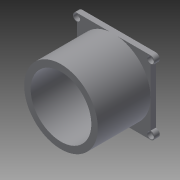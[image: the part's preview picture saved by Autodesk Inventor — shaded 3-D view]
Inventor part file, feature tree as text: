
AUTODESK INVENTOR PART (.ipt)
format: ipt  version: 2013 (Build 170138000, 138)  size: 433,664 bytes
history: native  units: in
note: dims shown in document units (in); Inventor stores cm internally (conversion verified against a paired STEP export)
features: extrude x14, sketch x14, reference x4, projected_geometry x1
ambient origin geometry x8: Origin, YZ Plane, XZ Plane, XY Plane, X Axis, Y Axis, Z Axis, Center Point
bodies: Solid1 (feature_tree)
feature tree (33):
  extrude  "Extrusion1"  Depth=0.1181in
  extrude  "Extrusion14"  Depth=0.1181in
  extrude  "Extrusion15"  Depth=0.1575in TaperAngle=0.0deg
  extrude  "Extrusion17"  Depth=0.0319in
  extrude  "Extrusion18"  Depth=0.1181in
  extrude  "Extrusion19"  Depth=0.1575in TaperAngle=0.0deg
  extrude  "Extrusion20"  Depth=1.5748in TaperAngle=0.0deg
  extrude  "Extrusion21"  Depth=1.811in
  extrude  "Extrusion22"  Depth=0.6339in
  extrude  "Extrusion23"  Depth=0.0394in
  extrude  "Extrusion24"  Depth=0.315in TaperAngle=0.0deg
  extrude  "Extrusion25"  Depth=0.2756in TaperAngle=0.0deg
  extrude  "Extrusion31"  Depth=0.2362in TaperAngle=0.0deg
  extrude  "Extrusion38"  Depth=0.1969in TaperAngle=0.0deg
  sketch  "Sketch40"  dims[d125=0.0394in d126=0.1969in d127=0.0in d128=0.0394in d129=0.1575in d130=0.0in d131=0.0394in d132=0.1181in d133=0.0in d134=0.0394in d135=0.0787in d136=0.0in d137=0.0394in d138=0.0394in d139=0.0in d172=0.1969in d174=0.1969in d175=0.1969in d176=0.1969in d177=0.1181in d178=0.0in d214=0.0in d215=0.1181in d216=0.0in d217=0.9843in d219=0.9843in d220=0.063in d221=0.0in]
  sketch  "Sketch1"  dims[d0=2.2in d2=0.1181in]
  reference  "Reference2"
  reference  "Reference3"
  reference  "Reference4"
  reference  "Reference5"
  sketch  "Sketch15"  dims[d3=0.2362in d4=0.1181in d5=0.2362in d6=1.95in]
  sketch  "Sketch17"  dims[d8=0.1181in d9=0.1575in d10=0.0in]
  sketch  "Sketch18"  dims[d11=0.1181in d12=0.1181in d14=0.0787in d33=0.0319in]
  sketch  "Sketch19"  dims[d35=0.3937in d36=0.5906in d37=0.7874in d38=0.9843in d39=0.3937in d40=0.5906in d41=1.1811in d42=1.378in d43=1.5748in d44=1.7717in d78=0.1181in]
  sketch  "Sketch20"  dims[d79=0.1181in d94=0.1575in d95=0.0in]
  sketch  "Sketch21"  dims[d96=1.811in d100=1.5748in d101=0.0in]
  sketch  "Sketch22"  dims[d102=2.2in d103=1.811in]
  sketch  "Sketch23"  dims[d111=0.8189in d112=0.6339in]
  sketch  "Sketch24"  dims[d113=0.4331in d114=0.0in d115=0.0394in]
  sketch  "Sketch25"  dims[d116=0.0394in d117=0.315in d118=0.0in]
  sketch  "Sketch31"  dims[d119=0.0394in d120=0.2756in d121=0.0in]
  projected_geometry  "Projected Loop2"
  sketch  "Sketch39"  dims[d122=0.0394in d123=0.2362in d124=0.0in]
